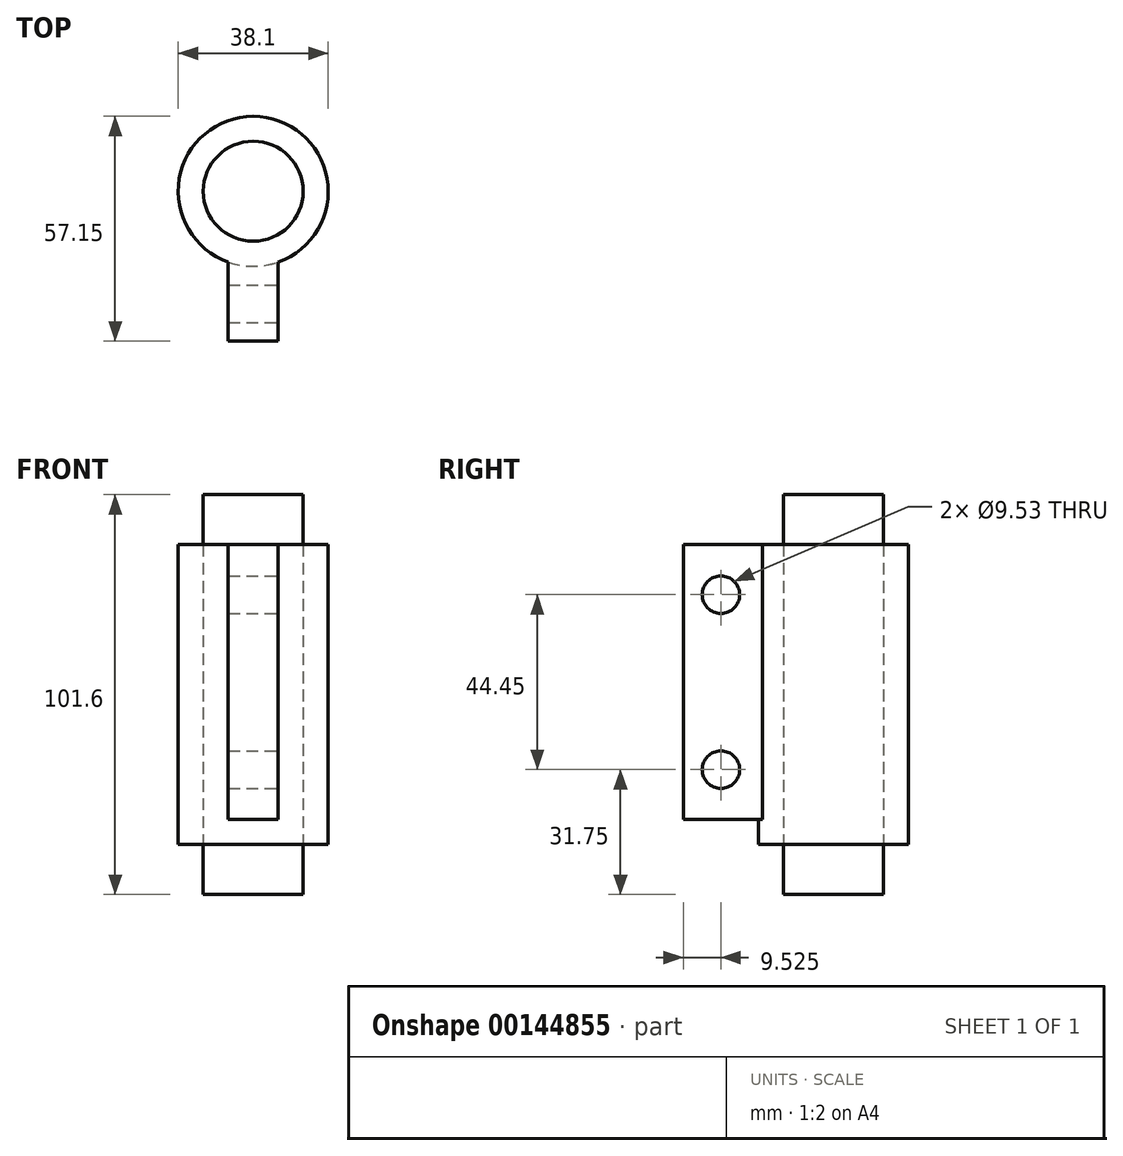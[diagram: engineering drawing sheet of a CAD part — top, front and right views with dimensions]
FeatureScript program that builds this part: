
annotation { "Feature Type Name" : "Feature", "Feature Type Description" : "" }
export const myFeature = defineFeature(function(context is Context, id is Id, definition is map)
    precondition{}
    {
        {
            var Q0;
            Q0=qCreatedBy(makeId("Top.planeOp"),FACE);
            var sketch = newSketch(context, id + "F0", { "sketchPlane" : qUnion([Q0])});
            skCircle(sketch, "E0", {"center": v(0, 0) * mm, "radius": 19.05 * mm});
            skSolve(sketch);
        }
        {
            var Q0;
            Q0=makeQuery(id+"F0.imprint","IMPRINT",FACE,{"disambiguationData":[TD([[makeQuery(id+"F0.imprint","IMPRINT",EDGE,{"derivedFrom":sQuery(id+"F0.wireOp",EDGE,"E0")}),1.0]])]});
            extrude(context, id + "F1", {"entities" : qUnion([Q0]), "endBound" : BoundingType.SYMMETRIC, "depth" : 76.2 * mm});
        }
        {
            var Q0;
            Q0=qCreatedBy(makeId("Front.planeOp"),FACE);
            var sketch = newSketch(context, id + "F2", { "sketchPlane" : qUnion([Q0])});
            skLineSegment(sketch, "E1.bottom", {"start": v(6.35, 38.1) * mm, "end": v(-6.35, 38.1) * mm});
            skLineSegment(sketch, "E1.top", {"start": v(6.35, -31.75) * mm, "end": v(-6.35, -31.75) * mm});
            skLineSegment(sketch, "E1.left", {"start": v(6.35, 38.1) * mm, "end": v(6.35, -31.75) * mm});
            skLineSegment(sketch, "E1.right", {"start": v(-6.35, 38.1) * mm, "end": v(-6.35, -31.75) * mm});
            skSolve(sketch);
        }
        {
            var Q0;
            Q0=qSketchRegion(id+"F2",true);
            extrude(context, id + "F3", {"entities" : qUnion([Q0]), "operationType" : NewBodyOperationType.ADD, "depth" : 38.1 * mm});
        }
        {
            var Q0;
            Q0=qCreatedBy(makeId("Right.planeOp"),FACE);
            var sketch = newSketch(context, id + "F4", { "sketchPlane" : qUnion([Q0])});
            skCircle(sketch, "E2", {"center": v(-28.58, 25.4) * mm, "radius": 4.76 * mm});
            skCircle(sketch, "E3", {"center": v(-28.57, -19.05) * mm, "radius": 4.76 * mm});
            skLineSegment(sketch, "E4", {"start": v(-28.57, 25.4) * mm, "end": v(-28.57, -19.05) * mm, "construction": true});
            skSolve(sketch);
        }
        {
            var Q0;
            Q0=qSketchRegion(id+"F4",true);
            extrude(context, id + "F5", {"entities" : qUnion([Q0]), "operationType" : NewBodyOperationType.REMOVE, "endBound" : BoundingType.SYMMETRIC, "oppositeDirection" : true, "depth" : 25.4 * mm});
        }
        {
            var Q0;
            Q0=qCreatedBy(makeId("Top.planeOp"),FACE);
            var sketch = newSketch(context, id + "F6", { "sketchPlane" : qUnion([Q0])});
            skCircle(sketch, "E5", {"center": v(0, 0) * mm, "radius": 12.7 * mm});
            skSolve(sketch);
        }
        {
            var Q0;
            Q0 = qSketchRegion(id + "F6", true);
            extrude(context, id + "F7", {"entities" : qUnion([Q0]), "endBound" : BoundingType.SYMMETRIC, "depth" : 101.6 * mm});
        }
    });
